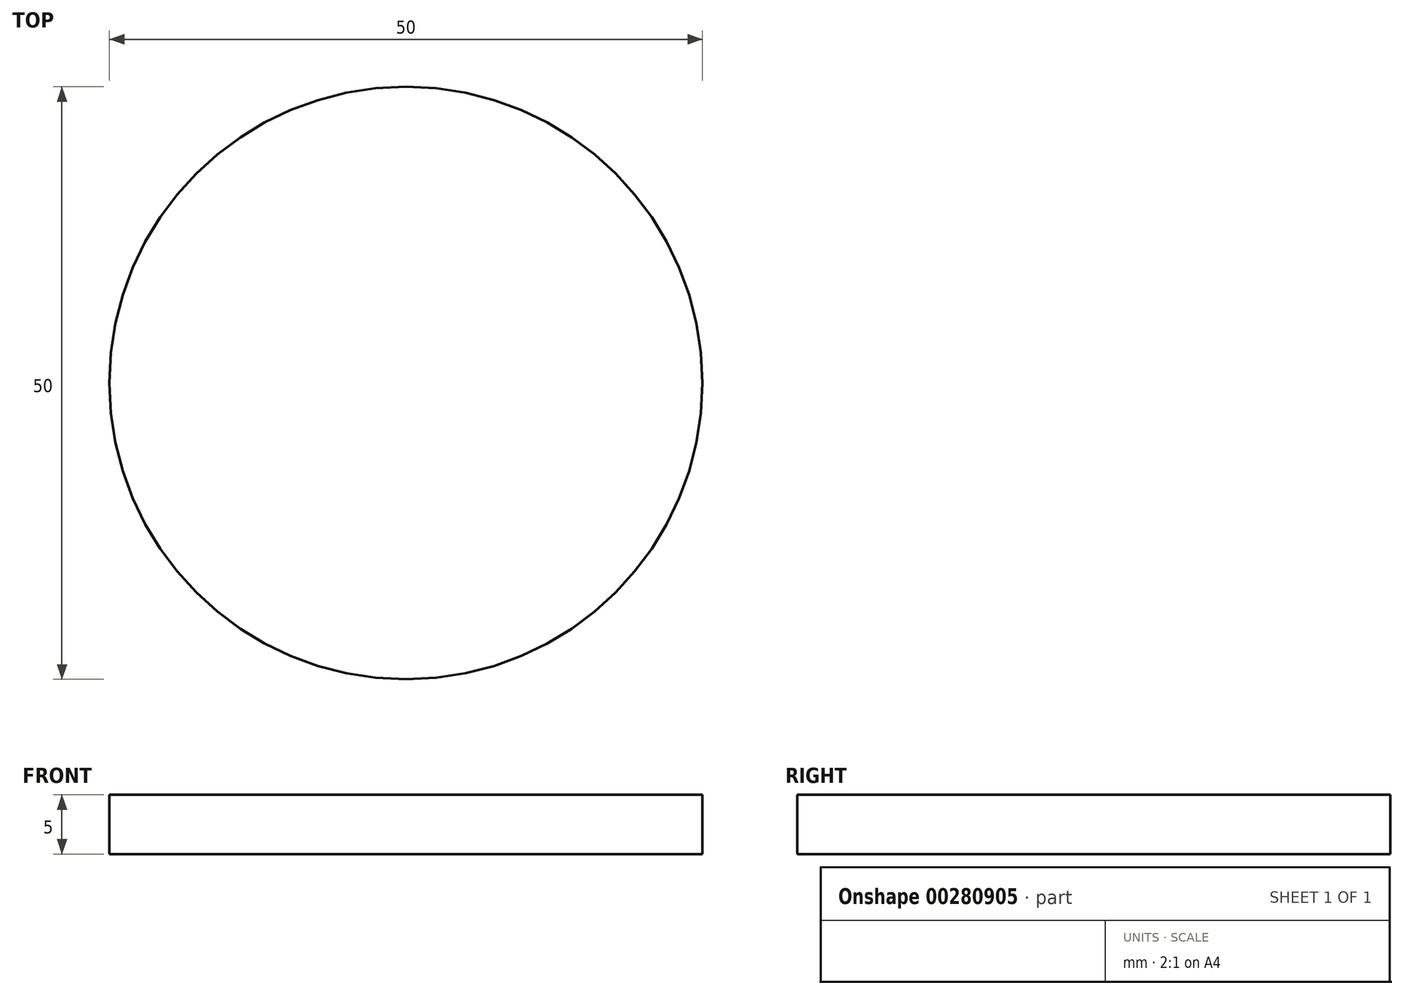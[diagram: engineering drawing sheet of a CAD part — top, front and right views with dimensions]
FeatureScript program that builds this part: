
annotation { "Feature Type Name" : "Feature", "Feature Type Description" : "" }
export const myFeature = defineFeature(function(context is Context, id is Id, definition is map)
    precondition{}
    {
        {
            var Q0;
            Q0=qCreatedBy(makeId("Top.planeOp"),FACE);
            var sketch = newSketch(context, id + "F0", { "sketchPlane" : qUnion([Q0])});
            skCircle(sketch, "E0", {"center": v(0, 0) * mm, "radius": 25 * mm});
            skLineSegment(sketch, "E1", {"start": v(0, -25) * mm, "end": v(0, -35) * mm});
            skLineSegment(sketch, "E2", {"start": v(25, 0) * mm, "end": v(35, 0) * mm});
            skLineSegment(sketch, "E3", {"start": v(0, 25) * mm, "end": v(0, 35) * mm});
            skLineSegment(sketch, "E4", {"start": v(-25, 0) * mm, "end": v(-35, 0) * mm});
            skLineSegment(sketch, "E5", {"start": v(0, 35) * mm, "end": v(4.53, 24.59) * mm});
            skLineSegment(sketch, "E6", {"start": v(35, 0) * mm, "end": v(24.59, -4.53) * mm});
            skLineSegment(sketch, "E7", {"start": v(0, -35) * mm, "end": v(4.53, -24.59) * mm});
            skLineSegment(sketch, "E8", {"start": v(0, -35) * mm, "end": v(-4.53, -24.59) * mm});
            skLineSegment(sketch, "E9", {"start": v(-35, 0) * mm, "end": v(-24.59, 4.53) * mm});
            skLineSegment(sketch, "E10", {"start": v(0, 35) * mm, "end": v(-4.53, 24.59) * mm});
            skLineSegment(sketch, "E11.trimOffspring", {"start": v(24.59, 4.53) * mm, "end": v(35, 0) * mm});
            skLineSegment(sketch, "E12.trimOffspring", {"start": v(-24.59, -4.53) * mm, "end": v(-35, 0) * mm});
            skSolve(sketch);
        }
        {
            var Q0;
            {var subQ0=sQuery(id+"F0.wireOp",EDGE,"E0");var subQ18=makeQuery(id+"F0.imprint","INTERSECT",VERTEX,{"derivedFrom":[subQ0,sQuery(id+"F0.wireOp",EDGE,"E2")]});Q0=makeQuery(id+"F0.imprint","IMPRINT",FACE,{"disambiguationData":[TD([[makeQuery(id+"F0.imprint","IMPRINT",EDGE,{"disambiguationData":[TD([[subQ18,-1.0]])],"derivedFrom":subQ0}),1.0]])]});}
            extrude(context, id + "F1", {"entities" : qUnion([Q0]), "depth" : 5 * mm});
        }
        {
            var Q0;
            Q0=qCreatedBy(makeId("Top.planeOp"),FACE);
            cPlane(context, id + "F2", {"entities" : qUnion([Q0]), "cplaneType" : CPlaneType.OFFSET, "offset" : 5 * mm, "width" : 150 * mm, "height" : 150 * mm});
        }
    });
